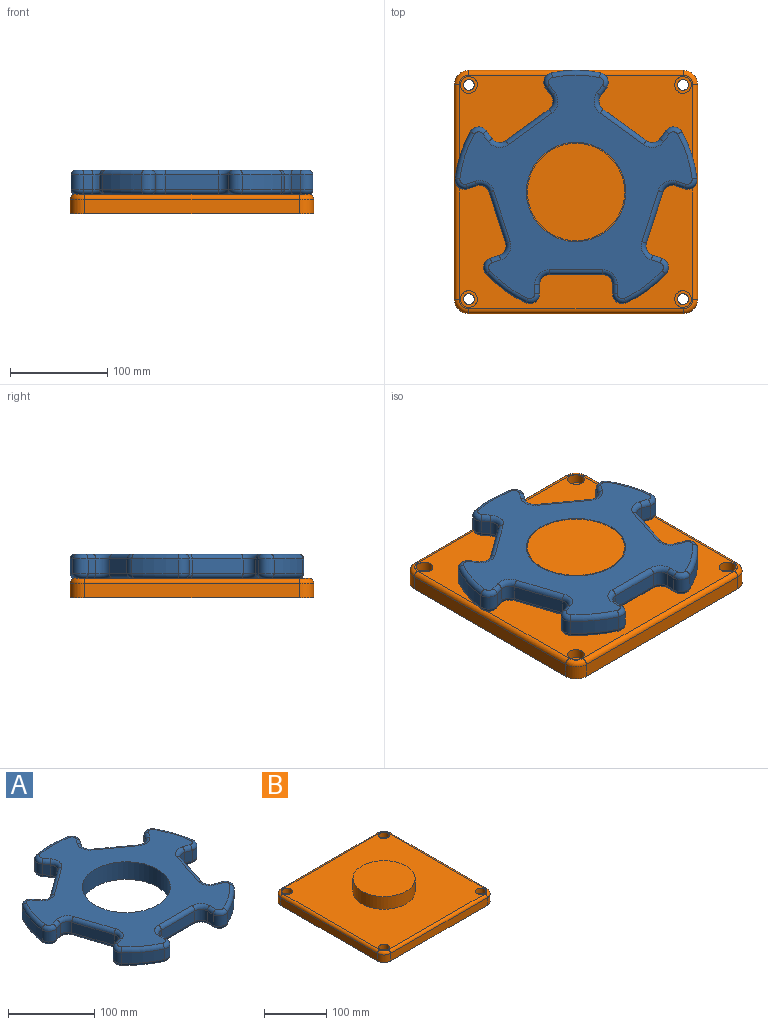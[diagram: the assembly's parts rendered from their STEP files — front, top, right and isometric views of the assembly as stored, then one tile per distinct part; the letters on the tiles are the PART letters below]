
ASSEMBLY  parts=2 mates=1
PART A: 123 faces, bbox 268.9x258.5x25 mm
  f0: plane 238.57x229.73mm, normal (0,0,1), area 21505.7mm2, adj f6,f43,f44,f45,f46,f47,f48,f49
  f1: plane 238.57x229.73mm, normal (0,0,-1), area 21505.7mm2, adj f6,f83,f84,f85,f86,f87,f88,f89
  f2: cylinder r=125mm len=40.68mm, axis (0,0,-1), area 759.5mm2, adj f13,f42,f51,f91
  f3: cylinder r=125mm len=47.82mm, axis (0,0,-1), area 759.5mm2, adj f35,f41,f67,f107
  f4: cylinder r=125mm len=50.29mm, axis (0,0,-1), area 759.5mm2, adj f28,f34,f82,f122
  f5: cylinder r=125mm len=47.82mm, axis (0,0,-1), area 759.5mm2, adj f21,f27,f66,f106
  f6: cylinder r=51mm len=102mm, axis (0,0,-1), area 8011.1mm2, adj f0,f1
  f7: cylinder r=125mm len=40.68mm, axis (0,0,-1), area 759.5mm2, adj f14,f20,f50,f90
  f8: plane 15x9.73mm, normal (-1,0,0), area 146mm2, adj f11,f14,f46,f86
  f9: plane 55x15mm, normal (0,-1,0), area 825mm2, adj f11,f12,f43,f83
  f10: plane 15x9.73mm, normal (1,0,0), area 146mm2, adj f12,f13,f47,f87
  f11: cylinder r=10mm len=15mm, axis (0,0,-1), area 235.6mm2, adj f8,f9,f44,f84
  f12: cylinder r=10mm len=15mm, axis (0,0,-1), area 235.6mm2, adj f9,f10,f45,f85
  f13: cylinder r=10mm len=15mm, axis (0,0,-1), area 299.5mm2, adj f2,f10,f49,f89
  f14: cylinder r=10mm len=15mm, axis (0,0,-1), area 299.5mm2, adj f7,f8,f48,f88
  f15: plane 15x9.26mm, normal (-0.31,-0.95,0), area 146mm2, adj f18,f21,f62,f102
  f16: plane 52.31x17mm, normal (0.95,-0.31,0), area 825mm2, adj f18,f19,f58,f98
  f17: plane 15x9.26mm, normal (0.31,0.95,0), area 146mm2, adj f19,f20,f54,f94
  f18: cylinder r=10mm len=15mm, axis (0,0,-1), area 235.6mm2, adj f15,f16,f60,f100
  f19: cylinder r=10mm len=15mm, axis (0,0,-1), area 235.6mm2, adj f16,f17,f56,f96
  f20: cylinder r=10mm len=16.25mm, axis (0,0,-1), area 299.5mm2, adj f7,f17,f52,f92
  f21: cylinder r=10mm len=15mm, axis (0,0,-1), area 299.5mm2, adj f5,f15,f64,f104
  f22: plane 15x7.87mm, normal (0.81,-0.59,0), area 146mm2, adj f25,f28,f78,f118
  f23: plane 44.5x32.33mm, normal (0.59,0.81,0), area 825mm2, adj f25,f26,f74,f114
  f24: plane 15x7.87mm, normal (-0.81,0.59,0), area 146mm2, adj f26,f27,f70,f110
  f25: cylinder r=10mm len=15mm, axis (0,0,-1), area 235.6mm2, adj f22,f23,f76,f116
  f26: cylinder r=10mm len=15mm, axis (0,0,-1), area 235.6mm2, adj f23,f24,f72,f112
  f27: cylinder r=10mm len=16.78mm, axis (0,0,-1), area 299.5mm2, adj f5,f24,f68,f108
  f28: cylinder r=10mm len=15.67mm, axis (0,0,-1), area 299.5mm2, adj f4,f22,f80,f120
  f29: plane 15x7.87mm, normal (0.81,0.59,0), area 146mm2, adj f32,f35,f71,f111
  f30: plane 44.5x32.33mm, normal (-0.59,0.81,0), area 825mm2, adj f32,f33,f75,f115
  f31: plane 15x7.87mm, normal (-0.81,-0.59,0), area 146mm2, adj f33,f34,f79,f119
  f32: cylinder r=10mm len=15mm, axis (0,0,-1), area 235.6mm2, adj f29,f30,f73,f113
  f33: cylinder r=10mm len=15mm, axis (0,0,-1), area 235.6mm2, adj f30,f31,f77,f117
  f34: cylinder r=10mm len=15.67mm, axis (0,0,-1), area 299.5mm2, adj f4,f31,f81,f121
  f35: cylinder r=10mm len=16.78mm, axis (0,0,-1), area 299.5mm2, adj f3,f29,f69,f109
  f36: plane 15x9.26mm, normal (-0.31,0.95,0), area 146mm2, adj f39,f42,f55,f95
  f37: plane 52.31x17mm, normal (-0.95,-0.31,0), area 825mm2, adj f39,f40,f59,f99
  f38: plane 15x9.26mm, normal (0.31,-0.95,0), area 146mm2, adj f40,f41,f63,f103
  f39: cylinder r=10mm len=15mm, axis (0,0,-1), area 235.6mm2, adj f36,f37,f57,f97
  f40: cylinder r=10mm len=15mm, axis (0,0,-1), area 235.6mm2, adj f37,f38,f61,f101
  f41: cylinder r=10mm len=15mm, axis (0,0,-1), area 299.5mm2, adj f3,f38,f65,f105
  f42: cylinder r=10mm len=16.25mm, axis (0,0,-1), area 299.5mm2, adj f2,f36,f53,f93
  f43: cylinder r=5mm len=55mm, axis (1,0,0), area 432mm2, adj f0,f9,f44,f45
  f44: torus R=15mm, axis (0,0,1), area 145.8mm2, adj f0,f11,f43,f46
  f45: torus R=15mm, axis (0,0,1), area 145.8mm2, adj f0,f12,f43,f47
  f46: cylinder r=5mm len=9.73mm, axis (0,-1,0), area 76.4mm2, adj f0,f8,f44,f48
  f47: cylinder r=5mm len=9.73mm, axis (0,1,0), area 76.4mm2, adj f0,f10,f45,f49
  f48: torus R=5mm, axis (0,0,1), area 128.3mm2, adj f0,f14,f46,f50
  f49: torus R=5mm, axis (0,0,1), area 128.3mm2, adj f0,f13,f47,f51
  f50: torus R=120mm, axis (0,0,1), area 391.9mm2, adj f0,f7,f48,f52
  f51: torus R=120mm, axis (0,0,1), area 391.9mm2, adj f0,f2,f49,f53
  f52: torus R=5mm, axis (0,0,1), area 128.3mm2, adj f0,f20,f50,f54
  f53: torus R=5mm, axis (0,0,1), area 128.3mm2, adj f0,f42,f51,f55
  f54: cylinder r=5mm len=10.8mm, axis (-0.95,0.31,0), area 76.4mm2, adj f0,f17,f52,f56
  f55: cylinder r=5mm len=10.8mm, axis (-0.95,-0.31,0), area 76.4mm2, adj f0,f36,f53,f57
  f56: torus R=15mm, axis (0,0,1), area 145.8mm2, adj f0,f19,f54,f58
  f57: torus R=15mm, axis (0,0,1), area 145.8mm2, adj f0,f39,f55,f59
  f58: cylinder r=5mm len=53.85mm, axis (0.31,0.95,0), area 432mm2, adj f0,f16,f56,f60
  f59: cylinder r=5mm len=53.85mm, axis (0.31,-0.95,0), area 432mm2, adj f0,f37,f57,f61
  f60: torus R=15mm, axis (0,0,1), area 145.8mm2, adj f0,f18,f58,f62
  f61: torus R=15mm, axis (0,0,1), area 145.8mm2, adj f0,f40,f59,f63
  f62: cylinder r=5mm len=10.8mm, axis (0.95,-0.31,0), area 76.4mm2, adj f0,f15,f60,f64
  f63: cylinder r=5mm len=10.8mm, axis (0.95,0.31,0), area 76.4mm2, adj f0,f38,f61,f65
  f64: torus R=5mm, axis (0,0,1), area 128.3mm2, adj f0,f21,f62,f66
  f65: torus R=5mm, axis (0,0,1), area 128.3mm2, adj f0,f41,f63,f67
  f66: torus R=120mm, axis (0,0,1), area 391.9mm2, adj f0,f5,f64,f68
  f67: torus R=120mm, axis (0,0,1), area 391.9mm2, adj f0,f3,f65,f69
  f68: torus R=5mm, axis (0,0,1), area 128.3mm2, adj f0,f27,f66,f70
  f69: torus R=5mm, axis (0,0,1), area 128.3mm2, adj f0,f35,f67,f71
  f70: cylinder r=5mm len=10.81mm, axis (-0.59,-0.81,0), area 76.4mm2, adj f0,f24,f68,f72
  f71: cylinder r=5mm len=10.81mm, axis (-0.59,0.81,0), area 76.4mm2, adj f0,f29,f69,f73
  f72: torus R=15mm, axis (0,0,1), area 145.8mm2, adj f0,f26,f70,f74
  f73: torus R=15mm, axis (0,0,1), area 145.8mm2, adj f0,f32,f71,f75
  f74: cylinder r=5mm len=47.44mm, axis (-0.81,0.59,0), area 432mm2, adj f0,f23,f72,f76
  f75: cylinder r=5mm len=47.44mm, axis (-0.81,-0.59,0), area 432mm2, adj f0,f30,f73,f77
  f76: torus R=15mm, axis (0,0,1), area 145.8mm2, adj f0,f25,f74,f78
  f77: torus R=15mm, axis (0,0,1), area 145.8mm2, adj f0,f33,f75,f79
  f78: cylinder r=5mm len=10.81mm, axis (0.59,0.81,0), area 76.4mm2, adj f0,f22,f76,f80
  f79: cylinder r=5mm len=10.81mm, axis (0.59,-0.81,0), area 76.4mm2, adj f0,f31,f77,f81
  f80: torus R=5mm, axis (0,0,1), area 128.3mm2, adj f0,f28,f78,f82
  f81: torus R=5mm, axis (0,0,1), area 128.3mm2, adj f0,f34,f79,f82
  f82: torus R=120mm, axis (0,0,1), area 391.9mm2, adj f0,f4,f80,f81
  f83: cylinder r=5mm len=55mm, axis (-1,0,0), area 432mm2, adj f1,f9,f84,f85
  f84: torus R=15mm, axis (0,0,1), area 145.8mm2, adj f1,f11,f83,f86
  f85: torus R=15mm, axis (0,0,1), area 145.8mm2, adj f1,f12,f83,f87
  f86: cylinder r=5mm len=9.73mm, axis (0,1,0), area 76.4mm2, adj f1,f8,f84,f88
  f87: cylinder r=5mm len=9.73mm, axis (0,-1,0), area 76.4mm2, adj f1,f10,f85,f89
  f88: torus R=5mm, axis (0,0,1), area 128.3mm2, adj f1,f14,f86,f90
  f89: torus R=5mm, axis (0,0,1), area 128.3mm2, adj f1,f13,f87,f91
  f90: torus R=120mm, axis (0,0,1), area 391.9mm2, adj f1,f7,f88,f92
  f91: torus R=120mm, axis (0,0,1), area 391.9mm2, adj f1,f2,f89,f93
  f92: torus R=5mm, axis (0,0,1), area 128.3mm2, adj f1,f20,f90,f94
  f93: torus R=5mm, axis (0,0,1), area 128.3mm2, adj f1,f42,f91,f95
  f94: cylinder r=5mm len=10.8mm, axis (0.95,-0.31,0), area 76.4mm2, adj f1,f17,f92,f96
  f95: cylinder r=5mm len=10.8mm, axis (0.95,0.31,0), area 76.4mm2, adj f1,f36,f93,f97
  f96: torus R=15mm, axis (0,0,1), area 145.8mm2, adj f1,f19,f94,f98
  f97: torus R=15mm, axis (0,0,1), area 145.8mm2, adj f1,f39,f95,f99
  f98: cylinder r=5mm len=53.85mm, axis (-0.31,-0.95,0), area 432mm2, adj f1,f16,f96,f100
  f99: cylinder r=5mm len=53.85mm, axis (-0.31,0.95,0), area 432mm2, adj f1,f37,f97,f101
  f100: torus R=15mm, axis (0,0,1), area 145.8mm2, adj f1,f18,f98,f102
  f101: torus R=15mm, axis (0,0,1), area 145.8mm2, adj f1,f40,f99,f103
  f102: cylinder r=5mm len=10.8mm, axis (-0.95,0.31,0), area 76.4mm2, adj f1,f15,f100,f104
  f103: cylinder r=5mm len=10.8mm, axis (-0.95,-0.31,0), area 76.4mm2, adj f1,f38,f101,f105
  f104: torus R=5mm, axis (0,0,1), area 128.3mm2, adj f1,f21,f102,f106
  f105: torus R=5mm, axis (0,0,1), area 128.3mm2, adj f1,f41,f103,f107
  f106: torus R=120mm, axis (0,0,1), area 391.9mm2, adj f1,f5,f104,f108
  f107: torus R=120mm, axis (0,0,1), area 391.9mm2, adj f1,f3,f105,f109
  f108: torus R=5mm, axis (0,0,1), area 128.3mm2, adj f1,f27,f106,f110
  f109: torus R=5mm, axis (0,0,1), area 128.3mm2, adj f1,f35,f107,f111
  f110: cylinder r=5mm len=10.81mm, axis (0.59,0.81,0), area 76.4mm2, adj f1,f24,f108,f112
  f111: cylinder r=5mm len=10.81mm, axis (0.59,-0.81,0), area 76.4mm2, adj f1,f29,f109,f113
  f112: torus R=15mm, axis (0,0,1), area 145.8mm2, adj f1,f26,f110,f114
  f113: torus R=15mm, axis (0,0,1), area 145.8mm2, adj f1,f32,f111,f115
  f114: cylinder r=5mm len=47.44mm, axis (0.81,-0.59,0), area 432mm2, adj f1,f23,f112,f116
  f115: cylinder r=5mm len=47.44mm, axis (0.81,0.59,0), area 432mm2, adj f1,f30,f113,f117
  f116: torus R=15mm, axis (0,0,1), area 145.8mm2, adj f1,f25,f114,f118
  f117: torus R=15mm, axis (0,0,1), area 145.8mm2, adj f1,f33,f115,f119
  f118: cylinder r=5mm len=10.81mm, axis (-0.59,-0.81,0), area 76.4mm2, adj f1,f22,f116,f120
  f119: cylinder r=5mm len=10.81mm, axis (-0.59,0.81,0), area 76.4mm2, adj f1,f31,f117,f121
  f120: torus R=5mm, axis (0,0,1), area 128.3mm2, adj f1,f28,f118,f122
  f121: torus R=5mm, axis (0,0,1), area 128.3mm2, adj f1,f34,f119,f122
  f122: torus R=120mm, axis (0,0,1), area 391.9mm2, adj f1,f4,f120,f121
PART B: 32 faces, bbox 252.5x252.5x45 mm
  f0: plane 220x15mm, normal (1,0,0), area 3300mm2, adj f5,f8,f11,f27
  f1: plane 220x15mm, normal (0,1,0), area 3300mm2, adj f5,f8,f9,f31
  f2: plane 220x15mm, normal (-1,0,0), area 3300mm2, adj f5,f9,f10,f28
  f3: plane 220x15mm, normal (0,-1,0), area 3300mm2, adj f5,f10,f11,f24
  f4: plane 240x240mm, normal (0,0,1), area 48725.4mm2, adj f6,f14,f17,f20,f23,f24,f25,f26
  f5: plane 250x250mm, normal (0,0,-1), area 61926.7mm2, adj f0,f1,f2,f3,f8,f9,f10,f11
  f6: cylinder r=50mm len=100mm, axis (0,0,-1), area 7854mm2, adj f4,f7
  f7: plane 100x100mm, normal (0,0,1), area 7854mm2, adj f6
  f8: cylinder r=15mm len=15mm, axis (0,0,-1), area 353.4mm2, adj f0,f1,f5,f29
  f9: cylinder r=15mm len=15mm, axis (0,0,1), area 353.4mm2, adj f1,f2,f5,f30
  f10: cylinder r=15mm len=15mm, axis (0,0,-1), area 353.4mm2, adj f2,f3,f5,f26
  f11: cylinder r=15mm len=15mm, axis (0,0,1), area 353.4mm2, adj f0,f3,f5,f25
  f12: cylinder r=5.5mm len=11mm, axis (0,0,1), area 345.6mm2, adj f5,f13
  f13: plane 17.25x17.25mm, normal (0,0,1), area 138.7mm2, adj f12,f14
  f14: cylinder r=8.62mm len=17.25mm, axis (0,0,1), area 541.9mm2, adj f4,f13
  f15: cylinder r=5.5mm len=11mm, axis (0,0,1), area 345.6mm2, adj f5,f16
  f16: plane 17.25x17.25mm, normal (0,0,1), area 138.7mm2, adj f15,f17
  f17: cylinder r=8.62mm len=17.25mm, axis (0,0,1), area 541.9mm2, adj f4,f16
  f18: cylinder r=5.5mm len=11mm, axis (0,0,1), area 345.6mm2, adj f5,f19
  f19: plane 17.25x17.25mm, normal (0,0,1), area 138.7mm2, adj f18,f20
  f20: cylinder r=8.62mm len=17.25mm, axis (0,0,1), area 541.9mm2, adj f4,f19
  f21: cylinder r=5.5mm len=11mm, axis (0,0,1), area 345.6mm2, adj f5,f22
  f22: plane 17.25x17.25mm, normal (0,0,1), area 138.7mm2, adj f21,f23
  f23: cylinder r=8.62mm len=17.25mm, axis (0,0,1), area 541.9mm2, adj f4,f22
  f24: cylinder r=5mm len=220mm, axis (-1,0,0), area 1727.9mm2, adj f3,f4,f25,f26
  f25: torus R=10mm, axis (0,0,1), area 162.6mm2, adj f4,f11,f24,f27
  f26: torus R=10mm, axis (0,0,1), area 162.6mm2, adj f4,f10,f24,f28
  f27: cylinder r=5mm len=220mm, axis (0,-1,0), area 1727.9mm2, adj f0,f4,f25,f29
  f28: cylinder r=5mm len=220mm, axis (0,1,0), area 1727.9mm2, adj f2,f4,f26,f30
  f29: torus R=10mm, axis (0,0,1), area 162.6mm2, adj f4,f8,f27,f31
  f30: torus R=10mm, axis (0,0,1), area 162.6mm2, adj f4,f9,f28,f31
  f31: cylinder r=5mm len=220mm, axis (1,0,0), area 1727.9mm2, adj f1,f4,f29,f30
PLACE A at identity
PLACE B at identity fixed
MATE revolute B.f6 <-> A.f2  axis (0,0,-1) through (0,0,32.5)mm
